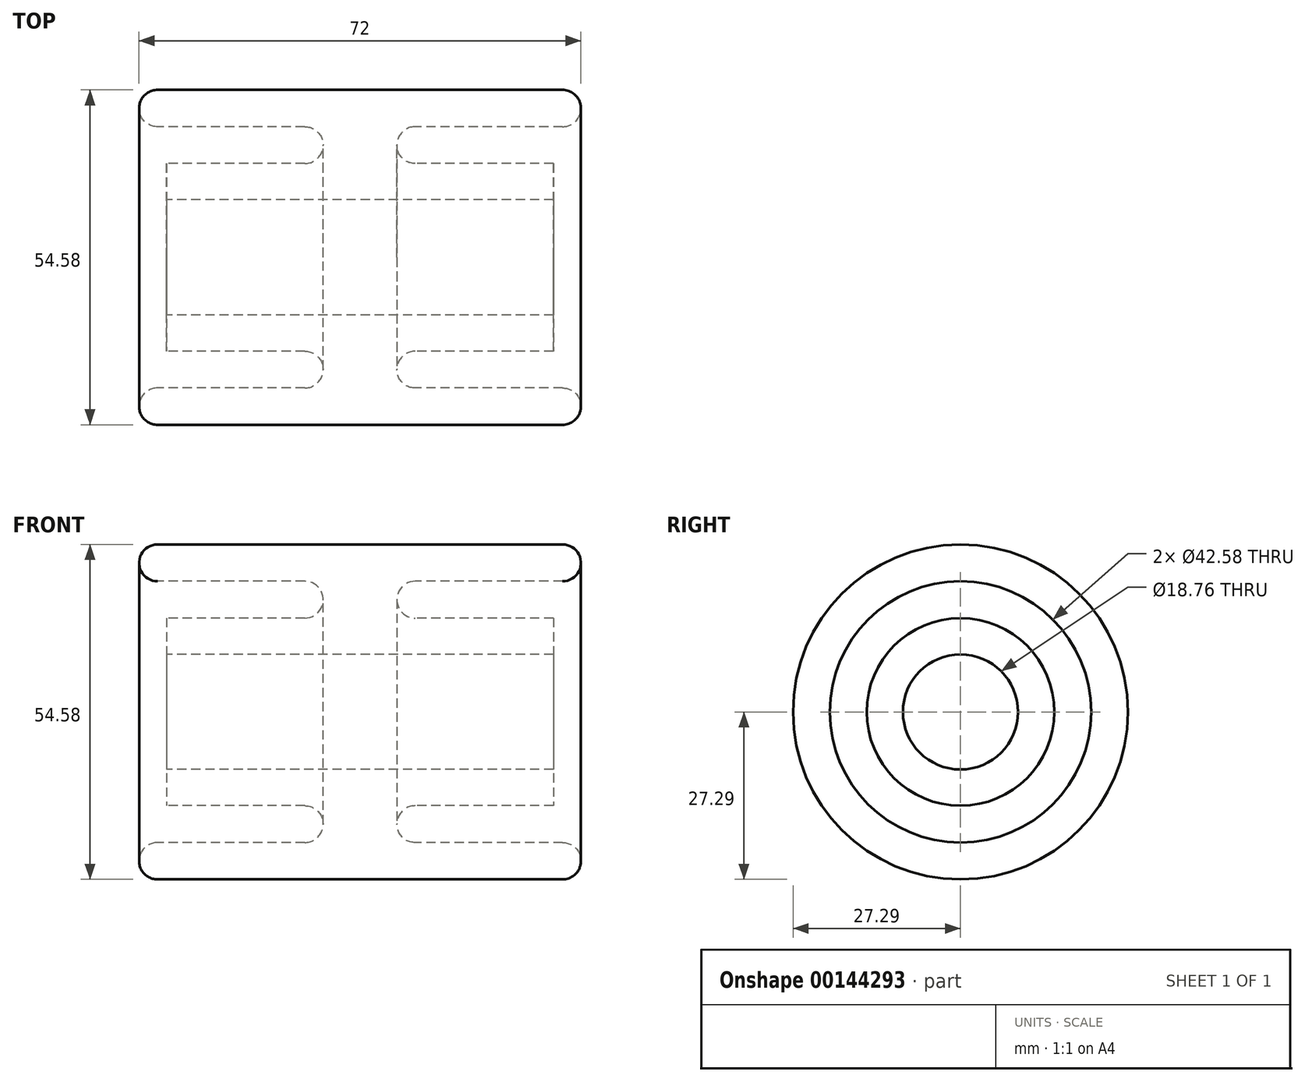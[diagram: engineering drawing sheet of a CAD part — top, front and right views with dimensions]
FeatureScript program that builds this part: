
annotation { "Feature Type Name" : "Feature", "Feature Type Description" : "" }
export const myFeature = defineFeature(function(context is Context, id is Id, definition is map)
    precondition{}
    {
        {
            var Q0;
            Q0=qCreatedBy(makeId("Front.planeOp"),FACE);
            var sketch = newSketch(context, id + "F0", { "sketchPlane" : qUnion([Q0])});
            skLineSegment(sketch, "E0", {"start": v(-34.02, 27.29) * mm, "end": v(31.98, 27.29) * mm});
            skArc(sketch, "E1", {"start": v(-34.02, 27.29) * mm, "mid": v(-37.02, 24.29) * mm, "end": v(-34.02, 21.29) * mm});
            skArc(sketch, "E2", {"start": v(31.98, 21.29) * mm, "mid": v(34.98, 24.29) * mm, "end": v(31.98, 27.29) * mm});
            skLineSegment(sketch, "E3", {"start": v(-34.02, 21.29) * mm, "end": v(-10.02, 21.29) * mm});
            skLineSegment(sketch, "E4", {"start": v(31.98, 21.29) * mm, "end": v(7.98, 21.29) * mm});
            skArc(sketch, "E5", {"start": v(-10.02, 15.29) * mm, "mid": v(-7.02, 18.29) * mm, "end": v(-10.02, 21.29) * mm});
            skArc(sketch, "E6", {"start": v(7.98, 21.29) * mm, "mid": v(4.98, 18.29) * mm, "end": v(7.98, 15.29) * mm});
            skLineSegment(sketch, "E7", {"start": v(-10.02, 15.29) * mm, "end": v(-32.52, 15.29) * mm});
            skLineSegment(sketch, "E8", {"start": v(7.98, 15.29) * mm, "end": v(30.48, 15.29) * mm});
            skLineSegment(sketch, "E9", {"start": v(-32.52, 15.29) * mm, "end": v(-32.52, 9.38) * mm});
            skLineSegment(sketch, "E10", {"start": v(-32.52, 9.38) * mm, "end": v(30.48, 9.38) * mm});
            skLineSegment(sketch, "E11", {"start": v(30.48, 9.38) * mm, "end": v(30.48, 15.29) * mm});
            skPoint(sketch, "E12", {"position": v(0, 0) * mm});
            skSolve(sketch);
        }
        {
            var Q0;
            Q0=qCreatedBy(makeId("Right.planeOp"),FACE);
            var sketch = newSketch(context, id + "F1", { "sketchPlane" : qUnion([Q0])});
            skCircle(sketch, "E13", {"center": v(0, 0) * mm, "radius": 22 * mm});
            skSolve(sketch);
        }
        {
            var Q0;
            Q0=makeQuery(id+"F0.imprint","IMPRINT",FACE,{"disambiguationData":[TD([[makeQuery(id+"F0.imprint","IMPRINT",EDGE,{"derivedFrom":sQuery(id+"F0.wireOp",EDGE,"E0")}),-1.0]])]});
            var Q1;
            Q1=sQuery(id+"F1.wireOp",EDGE,"E13");
            revolve(context, id + "F2", {"entities" : qUnion([Q0]), "axis" : qUnion([Q1]), "revolveType" : RevolveType.FULL});
        }
    });
